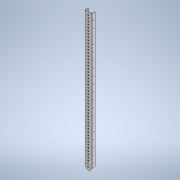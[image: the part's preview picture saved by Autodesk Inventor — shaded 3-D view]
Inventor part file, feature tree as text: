
AUTODESK INVENTOR PART (.ipt)
format: ipt  version: 2022 (Build 260153000, 153)  size: 270,848 bytes
history: native  units: mm
features: sketch x4, sheet_metal_op x3, extrude x3, projected_geometry x2, pattern_linear x1, other x1
ambient origin geometry x8: Origin, YZ Plane, XZ Plane, XY Plane, X Axis, Y Axis, Z Axis, Center Point
bodies: Solid1 (feature_tree)
feature tree (14):
  sheet_metal_op  "Contour Flange1"
  extrude  "Extrusion1"  Depth=50.0mm
  extrude  "Extrusion2"  Depth=1.5mm
  extrude  "Extrusion4"  Depth=1.5mm
  pattern_linear  "Rectangular Pattern1"  Spacing1=1.5mm  [1 undecoded]
  sketch  "Sketch1"  dims[d3=25.0mm d4=50.0mm]
  other  "Plate1"
  sheet_metal_op  "Bend1"
  sheet_metal_op  "Corner1"
  sketch  "Sketch2"  dims[d5=25.0mm d6=1.5mm]
  sketch  "Sketch3"  dims[d7=1.5mm d8=0.75mm]
  projected_geometry  "Projected Loop1"
  projected_geometry  "Projected Loop2"
  sketch  "Sketch5"  dims[d9=3.0mm d10=1.5mm d11=1000.0mm d12=1.5mm d13=1.5mm d14=6.0mm d15=1.5mm d16=1.5mm d17=20.0mm d18=10.0mm d19=25.0mm d20=490.0mm d22=20.0mm d23=10.0mm d25=10.0mm d27=0.0mm d28=0.0mm d29=0.0mm d30=0.0mm d33=3.35mm d34=11.0mm d35=28.0mm d36=0.0mm d37=0.0mm d38=190.0mm d40=50.0mm]
note: 1 required parameter value undecoded (feature->parameter linkage not recoverable at this tier; creation-order binding heuristic only, values carry confidence <= 0.55)
